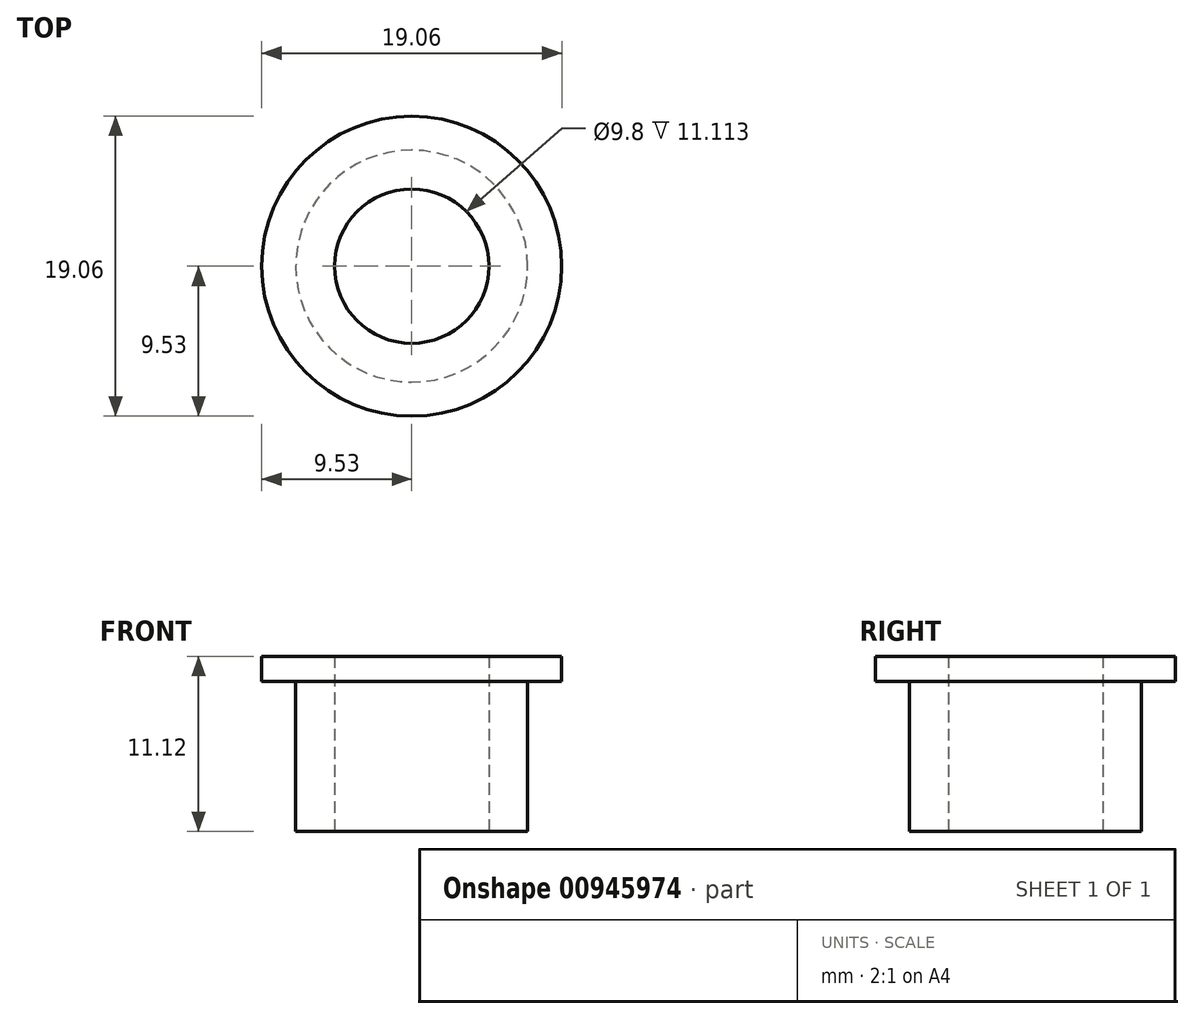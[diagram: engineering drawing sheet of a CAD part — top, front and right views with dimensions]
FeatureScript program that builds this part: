
annotation { "Feature Type Name" : "Feature", "Feature Type Description" : "" }
export const myFeature = defineFeature(function(context is Context, id is Id, definition is map)
    precondition{}
    {
        {
            var Q0;
            Q0=qCreatedBy(makeId("Top.planeOp"),FACE);
            cPlane(context, id + "F0", {"entities" : qUnion([Q0]), "cplaneType" : CPlaneType.OFFSET, "offset" : 9.52 * mm, "oppositeDirection" : true, "width" : 152.4 * mm, "height" : 152.4 * mm});
        }
        {
            var Q0;
            Q0=qCreatedBy(makeId("Top.planeOp"),FACE);
            cPlane(context, id + "F1", {"entities" : qUnion([Q0]), "cplaneType" : CPlaneType.OFFSET, "offset" : 1.59 * mm, "width" : 152.4 * mm, "height" : 152.4 * mm});
        }
        {
            var Q0;
            Q0=qCreatedBy(makeId("Top.planeOp"),FACE);
            var sketch = newSketch(context, id + "F2", { "sketchPlane" : qUnion([Q0])});
            skCircle(sketch, "E0", {"center": v(0, 0) * mm, "radius": 7.37 * mm});
            skSolve(sketch);
        }
        {
            var Q0;
            Q0 = qSketchRegion(id + "F2", true);
            var Q1;
            Q1=qCreatedBy(id+"F0.planeOp",FACE);
            extrude(context, id + "F3", {"entities" : qUnion([Q0]), "endBound" : BoundingType.UP_TO_SURFACE, "oppositeDirection" : true, "depth" : 25.4 * mm, "endBoundEntityFace" : qUnion([Q1]), "offsetDistance" : 25.4 * mm});
        }
        {
            var Q0;
            Q0=qCreatedBy(makeId("Top.planeOp"),FACE);
            var sketch = newSketch(context, id + "F4", { "sketchPlane" : qUnion([Q0])});
            skCircle(sketch, "E1", {"center": v(0, 0) * mm, "radius": 9.53 * mm});
            skSolve(sketch);
        }
        {
            var Q0;
            Q0=makeQuery(id+"F4.imprint","IMPRINT",FACE,{"disambiguationData":[TD([[makeQuery(id+"F4.imprint","IMPRINT",EDGE,{"derivedFrom":sQuery(id+"F4.wireOp",EDGE,"E1")}),1.0]])]});
            var Q1;
            Q1=qCreatedBy(id+"F1.planeOp",FACE);
            extrude(context, id + "F5", {"entities" : qUnion([Q0]), "operationType" : NewBodyOperationType.ADD, "endBound" : BoundingType.UP_TO_SURFACE, "depth" : 25.4 * mm, "endBoundEntityFace" : qUnion([Q1]), "offsetDistance" : 25.4 * mm});
        }
        {
            var Q0;
            Q0=qCreatedBy(makeId("Top.planeOp"),FACE);
            var sketch = newSketch(context, id + "F6", { "sketchPlane" : qUnion([Q0])});
            skLineSegment(sketch, "E2.bottom", {"start": v(19.05, -7.47) * mm, "end": v(-19.05, -7.47) * mm});
            skLineSegment(sketch, "E2.top", {"start": v(19.05, 7.47) * mm, "end": v(-19.05, 7.47) * mm});
            skLineSegment(sketch, "E2.left", {"start": v(19.05, -7.47) * mm, "end": v(19.05, 7.47) * mm, "construction": true});
            skLineSegment(sketch, "E2.right", {"start": v(-19.05, -7.47) * mm, "end": v(-19.05, 7.47) * mm, "construction": true});
            skPoint(sketch, "E2.middle", {"position": v(0, 0) * mm});
            skLineSegment(sketch, "E3.bottom", {"start": v(-19.05, 7.47) * mm, "end": v(19.05, 7.47) * mm});
            skLineSegment(sketch, "E3.top", {"start": v(-19.05, 22.4) * mm, "end": v(19.05, 22.4) * mm});
            skLineSegment(sketch, "E3.left", {"start": v(-19.05, 7.47) * mm, "end": v(-19.05, 22.4) * mm});
            skLineSegment(sketch, "E3.right", {"start": v(19.05, 7.47) * mm, "end": v(19.05, 22.4) * mm});
            skLineSegment(sketch, "E4.bottom", {"start": v(-19.05, -7.47) * mm, "end": v(19.05, -7.47) * mm});
            skLineSegment(sketch, "E4.top", {"start": v(-19.05, -22.4) * mm, "end": v(19.05, -22.4) * mm});
            skLineSegment(sketch, "E4.left", {"start": v(-19.05, -7.47) * mm, "end": v(-19.05, -22.4) * mm});
            skLineSegment(sketch, "E4.right", {"start": v(19.05, -7.47) * mm, "end": v(19.05, -22.4) * mm});
            skSolve(sketch);
        }
        {
            var Q0;
            Q0=qCreatedBy(id+"F0.planeOp",FACE);
            var sketch = newSketch(context, id + "F7", { "sketchPlane" : qUnion([Q0])});
            skPoint(sketch, "E5", {"position": v(0, 0) * mm});
            skSolve(sketch);
        }
        {
            var Q0;
            Q0=sQuery(id+"F7.wireOp",VERTEX,"E5");
            var Q1;
            Q1=makeQuery(id+"F3.opExtrude","SWEPT_BODY",BODY,{"disambiguationData":[OSD([sQuery(id+"F2.wireOp",EDGE,"E0")])]});
            hole(context, id + "F8", {"style" : HoleStyle.SIMPLE, "endStyle" : HoleEndStyle.THROUGH, "oppositeDirection" : true, "standardTappedOrClearance" : lookupTablePath({ "standard" : "ANSI", "size" : "W (0.39)", "type" : "Drilled" }), "standardBlindInLast" : lookupTablePath({ "standard" : "ANSI", "size" : "W (0.39)", "type" : "Drilled" }), "holeDiameter" : 9.8 * mm, "majorDiameter" : 6.35 * mm, "tappedDepth" : 12.7 * mm, "tapClearance" : 3, "locations" : qUnion([Q0]), "scope" : qUnion([Q1])});
        }
        {
            var Q0;
            Q0=sQuery(id+"F7.wireOp",VERTEX,"E5");
            var Q1;
            Q1=makeQuery(id+"F3.opExtrude","SWEPT_BODY",BODY,{"disambiguationData":[OSD([sQuery(id+"F2.wireOp",EDGE,"E0")])]});
            hole(context, id + "F9", {"style" : HoleStyle.SIMPLE, "endStyle" : HoleEndStyle.THROUGH, "oppositeDirection" : true, "standardTappedOrClearance" : lookupTablePath({ "standard" : "ANSI", "size" : "#21 (0.16)", "type" : "Drilled" }), "standardBlindInLast" : lookupTablePath({ "standard" : "ANSI", "size" : "#21 (0.16)", "type" : "Drilled" }), "holeDiameter" : 4.04 * mm, "majorDiameter" : 6.35 * mm, "tappedDepth" : 12.7 * mm, "tapClearance" : 3, "locations" : qUnion([Q0]), "scope" : qUnion([Q1])});
        }
    });
